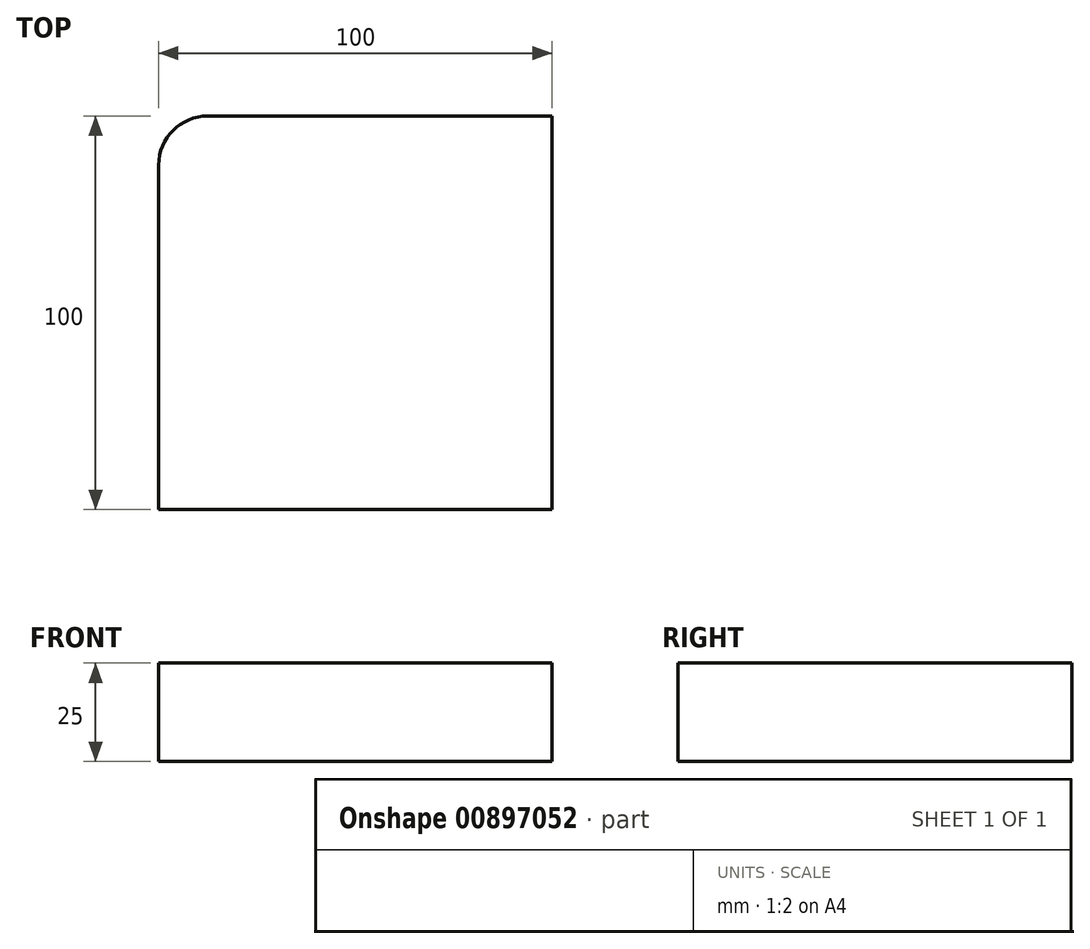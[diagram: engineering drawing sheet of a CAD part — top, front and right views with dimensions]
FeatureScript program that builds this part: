
annotation { "Feature Type Name" : "Feature", "Feature Type Description" : "" }
export const myFeature = defineFeature(function(context is Context, id is Id, definition is map)
    precondition{}
    {
        {
            var Q0;
            Q0=qCreatedBy(makeId("Top.planeOp"),FACE);
            var sketch = newSketch(context, id + "F0", { "sketchPlane" : qUnion([Q0])});
            skLineSegment(sketch, "E0.bottom", {"start": v(-37.5, 50) * mm, "end": v(50, 50) * mm});
            skLineSegment(sketch, "E0.top", {"start": v(-50, -50) * mm, "end": v(50, -50) * mm});
            skLineSegment(sketch, "E0.left", {"start": v(-50, 37.5) * mm, "end": v(-50, -50) * mm});
            skLineSegment(sketch, "E0.right", {"start": v(50, 50) * mm, "end": v(50, -50) * mm});
            skPoint(sketch, "E0.middle", {"position": v(0, 0) * mm});
            skArc(sketch, "E1", {"start": v(-37.5, 50) * mm, "mid": v(-46.34, 46.34) * mm, "end": v(-50, 37.5) * mm});
            skPoint(sketch, "E2.orphan", {"position": v(-50, 50) * mm});
            skSolve(sketch);
        }
        {
            var Q0;
            Q0=makeQuery(id+"F0.imprint","IMPRINT",FACE,{"disambiguationData":[TD([[makeQuery(id+"F0.imprint","IMPRINT",EDGE,{"derivedFrom":sQuery(id+"F0.wireOp",EDGE,"E0.bottom")}),-1.0]])]});
            extrude(context, id + "F1", {"entities" : qUnion([Q0]), "depth" : 25 * mm, "offsetDistance" : 25 * mm});
        }
    });
